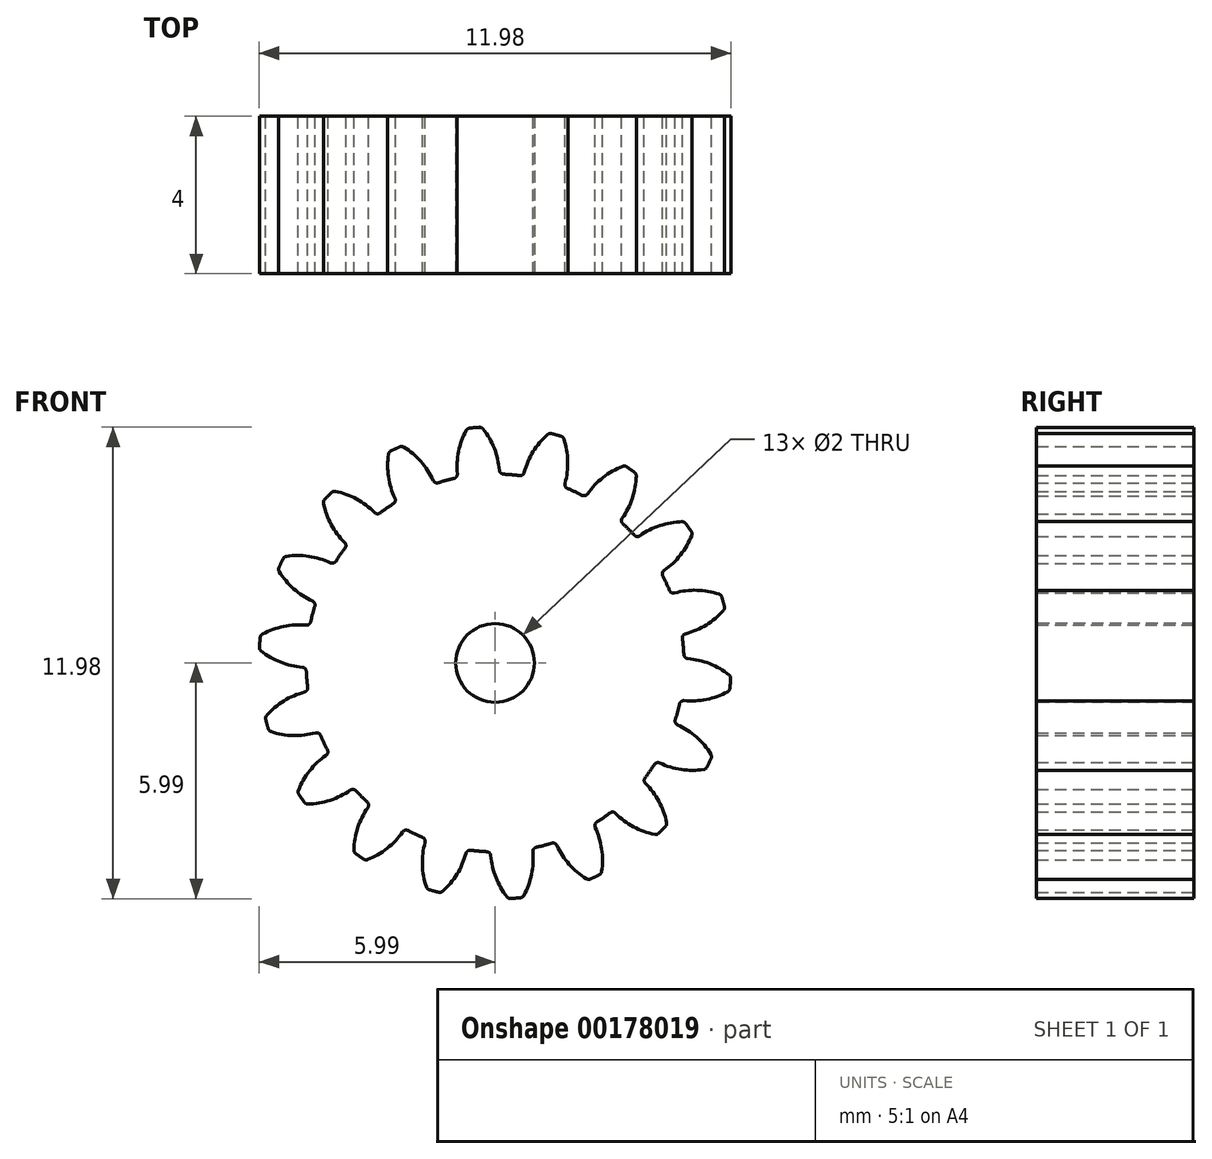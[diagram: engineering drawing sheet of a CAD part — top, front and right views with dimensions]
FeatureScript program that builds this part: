
annotation { "Feature Type Name" : "Feature", "Feature Type Description" : "" }
export const myFeature = defineFeature(function(context is Context, id is Id, definition is map)
    precondition{}
    {
        {
            var Q0;
            Q0=qCreatedBy(makeId("Front.planeOp"),FACE);
            var sketch = newSketch(context, id + "F0", { "sketchPlane" : qUnion([Q0])});
            skCircle(sketch, "E0", {"center": v(0, 0) * mm, "radius": 4.8 * mm, "construction": true});
            skCircle(sketch, "E1", {"center": v(0, 0) * mm, "radius": 5.4 * mm, "construction": true});
            skCircle(sketch, "E2", {"center": v(0, 0) * mm, "radius": 6 * mm, "construction": true});
            skLineSegment(sketch, "E3", {"start": v(0, 0) * mm, "end": v(0, 8.87) * mm, "construction": true});
            skCircle(sketch, "E4.cCircle", {"center": v(0, 0) * mm, "radius": 8.87 * mm, "construction": true});
            skLineSegment(sketch, "E4.0", {"start": v(-0.78, 8.87) * mm, "end": v(0.78, 8.87) * mm, "construction": true});
            skLineSegment(sketch, "E4.1", {"start": v(0.78, 8.87) * mm, "end": v(2.3, 8.6) * mm, "construction": true});
            skLineSegment(sketch, "E4.2", {"start": v(2.3, 8.6) * mm, "end": v(3.76, 8.07) * mm, "construction": true});
            skLineSegment(sketch, "E4.3", {"start": v(3.76, 8.07) * mm, "end": v(5.1, 7.3) * mm, "construction": true});
            skLineSegment(sketch, "E4.4", {"start": v(5.1, 7.3) * mm, "end": v(6.3, 6.3) * mm, "construction": true});
            skLineSegment(sketch, "E4.5", {"start": v(6.3, 6.3) * mm, "end": v(7.3, 5.1) * mm, "construction": true});
            skLineSegment(sketch, "E4.6", {"start": v(7.3, 5.1) * mm, "end": v(8.07, 3.76) * mm, "construction": true});
            skLineSegment(sketch, "E4.7", {"start": v(8.07, 3.76) * mm, "end": v(8.6, 2.3) * mm, "construction": true});
            skLineSegment(sketch, "E4.8", {"start": v(8.6, 2.3) * mm, "end": v(8.87, 0.78) * mm, "construction": true});
            skLineSegment(sketch, "E4.9", {"start": v(8.87, 0.78) * mm, "end": v(8.87, -0.78) * mm, "construction": true});
            skLineSegment(sketch, "E4.10", {"start": v(8.87, -0.78) * mm, "end": v(8.6, -2.3) * mm, "construction": true});
            skLineSegment(sketch, "E4.11", {"start": v(8.6, -2.3) * mm, "end": v(8.07, -3.76) * mm, "construction": true});
            skLineSegment(sketch, "E4.12", {"start": v(8.07, -3.76) * mm, "end": v(7.3, -5.1) * mm, "construction": true});
            skLineSegment(sketch, "E4.13", {"start": v(7.3, -5.1) * mm, "end": v(6.3, -6.3) * mm, "construction": true});
            skLineSegment(sketch, "E4.14", {"start": v(6.3, -6.3) * mm, "end": v(5.1, -7.3) * mm, "construction": true});
            skLineSegment(sketch, "E4.15", {"start": v(5.1, -7.3) * mm, "end": v(3.76, -8.07) * mm, "construction": true});
            skLineSegment(sketch, "E4.16", {"start": v(3.76, -8.07) * mm, "end": v(2.3, -8.6) * mm, "construction": true});
            skLineSegment(sketch, "E4.17", {"start": v(2.3, -8.6) * mm, "end": v(0.78, -8.87) * mm, "construction": true});
            skLineSegment(sketch, "E4.18", {"start": v(0.78, -8.87) * mm, "end": v(-0.78, -8.87) * mm, "construction": true});
            skLineSegment(sketch, "E4.19", {"start": v(-0.78, -8.87) * mm, "end": v(-2.3, -8.6) * mm, "construction": true});
            skLineSegment(sketch, "E4.20", {"start": v(-2.3, -8.6) * mm, "end": v(-3.76, -8.07) * mm, "construction": true});
            skLineSegment(sketch, "E4.21", {"start": v(-3.76, -8.07) * mm, "end": v(-5.1, -7.3) * mm, "construction": true});
            skLineSegment(sketch, "E4.22", {"start": v(-5.1, -7.3) * mm, "end": v(-6.3, -6.3) * mm, "construction": true});
            skLineSegment(sketch, "E4.23", {"start": v(-6.3, -6.3) * mm, "end": v(-7.3, -5.1) * mm, "construction": true});
            skLineSegment(sketch, "E4.24", {"start": v(-7.3, -5.1) * mm, "end": v(-8.07, -3.76) * mm, "construction": true});
            skLineSegment(sketch, "E4.25", {"start": v(-8.07, -3.76) * mm, "end": v(-8.6, -2.3) * mm, "construction": true});
            skLineSegment(sketch, "E4.26", {"start": v(-8.6, -2.3) * mm, "end": v(-8.87, -0.78) * mm, "construction": true});
            skLineSegment(sketch, "E4.27", {"start": v(-8.87, -0.78) * mm, "end": v(-8.87, 0.78) * mm, "construction": true});
            skLineSegment(sketch, "E4.28", {"start": v(-8.87, 0.78) * mm, "end": v(-8.6, 2.3) * mm, "construction": true});
            skLineSegment(sketch, "E4.29", {"start": v(-8.6, 2.3) * mm, "end": v(-8.07, 3.76) * mm, "construction": true});
            skLineSegment(sketch, "E4.30", {"start": v(-8.07, 3.76) * mm, "end": v(-7.3, 5.1) * mm, "construction": true});
            skLineSegment(sketch, "E4.31", {"start": v(-7.3, 5.1) * mm, "end": v(-6.3, 6.3) * mm, "construction": true});
            skLineSegment(sketch, "E4.32", {"start": v(-6.3, 6.3) * mm, "end": v(-5.1, 7.3) * mm, "construction": true});
            skLineSegment(sketch, "E4.33", {"start": v(-5.1, 7.3) * mm, "end": v(-3.76, 8.07) * mm, "construction": true});
            skLineSegment(sketch, "E4.34", {"start": v(-3.76, 8.07) * mm, "end": v(-2.3, 8.6) * mm, "construction": true});
            skLineSegment(sketch, "E4.35", {"start": v(-2.3, 8.6) * mm, "end": v(-0.78, 8.87) * mm, "construction": true});
            skPoint(sketch, "E4.0.midPoint", {"position": v(0, 8.87) * mm});
            skLineSegment(sketch, "E5.0", {"start": v(0, 8.87) * mm, "end": v(1.58, 8.72) * mm, "construction": true});
            skLineSegment(sketch, "E5.1", {"start": v(1.58, 8.72) * mm, "end": v(3.12, 8.3) * mm, "construction": true});
            skLineSegment(sketch, "E5.2", {"start": v(3.12, 8.3) * mm, "end": v(4.55, 7.61) * mm, "construction": true});
            skLineSegment(sketch, "E5.3", {"start": v(4.55, 7.61) * mm, "end": v(5.83, 6.68) * mm, "construction": true});
            skLineSegment(sketch, "E5.4", {"start": v(5.83, 6.68) * mm, "end": v(6.93, 5.53) * mm, "construction": true});
            skLineSegment(sketch, "E5.5", {"start": v(6.93, 5.53) * mm, "end": v(7.8, 4.2) * mm, "construction": true});
            skLineSegment(sketch, "E5.6", {"start": v(7.8, 4.2) * mm, "end": v(8.43, 2.74) * mm, "construction": true});
            skLineSegment(sketch, "E5.7", {"start": v(8.43, 2.74) * mm, "end": v(8.79, 1.2) * mm, "construction": true});
            skLineSegment(sketch, "E5.8", {"start": v(8.79, 1.2) * mm, "end": v(8.86, -0.4) * mm, "construction": true});
            skLineSegment(sketch, "E5.9", {"start": v(8.86, -0.4) * mm, "end": v(8.65, -1.97) * mm, "construction": true});
            skLineSegment(sketch, "E5.10", {"start": v(8.65, -1.97) * mm, "end": v(8.15, -3.49) * mm, "construction": true});
            skLineSegment(sketch, "E5.11", {"start": v(8.15, -3.49) * mm, "end": v(7.4, -4.88) * mm, "construction": true});
            skLineSegment(sketch, "E5.12", {"start": v(7.4, -4.88) * mm, "end": v(6.4, -6.13) * mm, "construction": true});
            skLineSegment(sketch, "E5.13", {"start": v(6.4, -6.13) * mm, "end": v(5.21, -7.17) * mm, "construction": true});
            skLineSegment(sketch, "E5.14", {"start": v(5.21, -7.17) * mm, "end": v(3.85, -7.99) * mm, "construction": true});
            skLineSegment(sketch, "E5.15", {"start": v(3.85, -7.99) * mm, "end": v(2.36, -8.55) * mm, "construction": true});
            skLineSegment(sketch, "E5.16", {"start": v(2.36, -8.55) * mm, "end": v(0.8, -8.83) * mm, "construction": true});
            skLineSegment(sketch, "E5.17", {"start": v(0.8, -8.83) * mm, "end": v(-0.8, -8.83) * mm, "construction": true});
            skLineSegment(sketch, "E5.18", {"start": v(-0.8, -8.83) * mm, "end": v(-2.36, -8.55) * mm, "construction": true});
            skLineSegment(sketch, "E5.19", {"start": v(-2.36, -8.55) * mm, "end": v(-3.85, -7.99) * mm, "construction": true});
            skLineSegment(sketch, "E5.20", {"start": v(-3.85, -7.99) * mm, "end": v(-5.21, -7.17) * mm, "construction": true});
            skLineSegment(sketch, "E5.21", {"start": v(-5.21, -7.17) * mm, "end": v(-6.4, -6.13) * mm, "construction": true});
            skLineSegment(sketch, "E5.22", {"start": v(-6.4, -6.13) * mm, "end": v(-7.4, -4.88) * mm, "construction": true});
            skLineSegment(sketch, "E5.23", {"start": v(-7.4, -4.88) * mm, "end": v(-8.15, -3.49) * mm, "construction": true});
            skLineSegment(sketch, "E5.24", {"start": v(-8.15, -3.49) * mm, "end": v(-8.65, -1.97) * mm, "construction": true});
            skLineSegment(sketch, "E5.25", {"start": v(-8.65, -1.97) * mm, "end": v(-8.86, -0.4) * mm, "construction": true});
            skLineSegment(sketch, "E5.26", {"start": v(-8.86, -0.4) * mm, "end": v(-8.79, 1.2) * mm, "construction": true});
            skLineSegment(sketch, "E5.27", {"start": v(-8.79, 1.2) * mm, "end": v(-8.43, 2.74) * mm, "construction": true});
            skLineSegment(sketch, "E5.28", {"start": v(-8.43, 2.74) * mm, "end": v(-7.8, 4.2) * mm, "construction": true});
            skLineSegment(sketch, "E5.29", {"start": v(-7.8, 4.2) * mm, "end": v(-6.93, 5.53) * mm, "construction": true});
            skLineSegment(sketch, "E5.30", {"start": v(-6.93, 5.53) * mm, "end": v(-5.83, 6.68) * mm, "construction": true});
            skLineSegment(sketch, "E5.31", {"start": v(-5.83, 6.68) * mm, "end": v(-4.55, 7.61) * mm, "construction": true});
            skLineSegment(sketch, "E5.32", {"start": v(-4.55, 7.61) * mm, "end": v(-3.12, 8.3) * mm, "construction": true});
            skLineSegment(sketch, "E5.33", {"start": v(-3.12, 8.3) * mm, "end": v(-1.58, 8.72) * mm, "construction": true});
            skLineSegment(sketch, "E5.34", {"start": v(-1.58, 8.72) * mm, "end": v(0, 8.87) * mm, "construction": true});
            skLineSegment(sketch, "E6", {"start": v(0, 0) * mm, "end": v(-0.78, 8.87) * mm, "construction": true});
            skLineSegment(sketch, "E7", {"start": v(0, 5.4) * mm, "end": v(-9.47, 5.4) * mm, "construction": true});
            skLineSegment(sketch, "E8", {"start": v(0, 5.4) * mm, "end": v(-9.34, 2) * mm, "construction": true});
            skCircle(sketch, "E9", {"center": v(0, 5.4) * mm, "radius": 1.94 * mm, "construction": true});
            skCircle(sketch, "E10", {"center": v(-1.83, 4.74) * mm, "radius": 1.94 * mm, "construction": true});
            skArc(sketch, "E11", {"start": v(-0.3, 5.95) * mm, "mid": v(-0.02, 5.45) * mm, "end": v(0.11, 4.9) * mm});
            skArc(sketch, "E12.MirrorCS", {"start": v(-0.73, 5.9) * mm, "mid": v(-0.93, 5.37) * mm, "end": v(-0.96, 4.8) * mm});
            skArc(sketch, "E13", {"start": v(-0.65, 5.96) * mm, "mid": v(-0.52, 5.98) * mm, "end": v(-0.4, 5.99) * mm});
            skArc(sketch, "E14", {"start": v(-1.04, 4.69) * mm, "mid": v(0.42, -4.78) * mm, "end": v(0.21, 4.8) * mm});
            skPoint(sketch, "E15.visualSharp", {"position": v(-0.95, 4.7) * mm});
            skArc(sketch, "E15.filletArc", {"start": v(-1.04, 4.69) * mm, "mid": v(-0.98, 4.73) * mm, "end": v(-0.96, 4.8) * mm});
            skPoint(sketch, "E16.visualSharp", {"position": v(0.12, 4.8) * mm});
            skArc(sketch, "E16.filletArc", {"start": v(0.11, 4.9) * mm, "mid": v(0.14, 4.83) * mm, "end": v(0.21, 4.8) * mm});
            skPoint(sketch, "E17.visualSharp", {"position": v(-0.7, 5.96) * mm});
            skArc(sketch, "E17.filletArc", {"start": v(-0.65, 5.96) * mm, "mid": v(-0.7, 5.95) * mm, "end": v(-0.73, 5.9) * mm});
            skPoint(sketch, "E18.visualSharp", {"position": v(-0.34, 6) * mm});
            skArc(sketch, "E18.filletArc", {"start": v(-0.3, 5.95) * mm, "mid": v(-0.35, 5.98) * mm, "end": v(-0.4, 5.99) * mm});
            skArc(sketch, "E19.1.0", {"start": v(-2.58, 4.05) * mm, "mid": v(-2.54, 4.1) * mm, "end": v(-2.54, 4.18) * mm});
            skArc(sketch, "E19.1.1", {"start": v(-2.7, 5.3) * mm, "mid": v(-2.7, 4.73) * mm, "end": v(-2.54, 4.18) * mm});
            skArc(sketch, "E19.1.2", {"start": v(-2.65, 5.38) * mm, "mid": v(-2.69, 5.35) * mm, "end": v(-2.7, 5.3) * mm});
            skArc(sketch, "E19.1.3", {"start": v(-2.65, 5.38) * mm, "mid": v(-2.54, 5.44) * mm, "end": v(-2.42, 5.49) * mm});
            skArc(sketch, "E19.1.4", {"start": v(-2.32, 5.48) * mm, "mid": v(-2.37, 5.5) * mm, "end": v(-2.42, 5.49) * mm});
            skArc(sketch, "E19.1.5", {"start": v(-2.32, 5.48) * mm, "mid": v(-1.88, 5.12) * mm, "end": v(-1.57, 4.64) * mm});
            skArc(sketch, "E19.1.6", {"start": v(-1.57, 4.64) * mm, "mid": v(-1.52, 4.58) * mm, "end": v(-1.44, 4.58) * mm});
            skArc(sketch, "E19.2.0", {"start": v(-3.81, 2.92) * mm, "mid": v(-3.79, 3) * mm, "end": v(-3.82, 3.06) * mm});
            skArc(sketch, "E19.2.1", {"start": v(-4.36, 4.06) * mm, "mid": v(-4.16, 3.52) * mm, "end": v(-3.82, 3.06) * mm});
            skArc(sketch, "E19.2.2", {"start": v(-4.33, 4.15) * mm, "mid": v(-4.36, 4.1) * mm, "end": v(-4.36, 4.06) * mm});
            skArc(sketch, "E19.2.3", {"start": v(-4.33, 4.15) * mm, "mid": v(-4.24, 4.24) * mm, "end": v(-4.15, 4.33) * mm});
            skArc(sketch, "E19.2.4", {"start": v(-4.06, 4.36) * mm, "mid": v(-4.1, 4.36) * mm, "end": v(-4.15, 4.33) * mm});
            skArc(sketch, "E19.2.5", {"start": v(-4.06, 4.36) * mm, "mid": v(-3.52, 4.16) * mm, "end": v(-3.06, 3.82) * mm});
            skArc(sketch, "E19.2.6", {"start": v(-3.06, 3.82) * mm, "mid": v(-3, 3.79) * mm, "end": v(-2.92, 3.81) * mm});
            skArc(sketch, "E19.3.0", {"start": v(-4.58, 1.44) * mm, "mid": v(-4.58, 1.52) * mm, "end": v(-4.64, 1.57) * mm});
            skArc(sketch, "E19.3.1", {"start": v(-5.48, 2.32) * mm, "mid": v(-5.12, 1.88) * mm, "end": v(-4.64, 1.57) * mm});
            skArc(sketch, "E19.3.2", {"start": v(-5.49, 2.42) * mm, "mid": v(-5.5, 2.37) * mm, "end": v(-5.48, 2.32) * mm});
            skArc(sketch, "E19.3.3", {"start": v(-5.49, 2.42) * mm, "mid": v(-5.44, 2.54) * mm, "end": v(-5.38, 2.65) * mm});
            skArc(sketch, "E19.3.4", {"start": v(-5.3, 2.7) * mm, "mid": v(-5.35, 2.69) * mm, "end": v(-5.38, 2.65) * mm});
            skArc(sketch, "E19.3.5", {"start": v(-5.3, 2.7) * mm, "mid": v(-4.73, 2.7) * mm, "end": v(-4.18, 2.54) * mm});
            skArc(sketch, "E19.3.6", {"start": v(-4.18, 2.54) * mm, "mid": v(-4.1, 2.54) * mm, "end": v(-4.05, 2.58) * mm});
            skArc(sketch, "E19.4.0", {"start": v(-4.8, -0.21) * mm, "mid": v(-4.83, -0.14) * mm, "end": v(-4.9, -0.11) * mm});
            skArc(sketch, "E19.4.1", {"start": v(-5.95, 0.3) * mm, "mid": v(-5.45, 0.02) * mm, "end": v(-4.9, -0.11) * mm});
            skArc(sketch, "E19.4.2", {"start": v(-5.99, 0.4) * mm, "mid": v(-5.98, 0.35) * mm, "end": v(-5.95, 0.3) * mm});
            skArc(sketch, "E19.4.3", {"start": v(-5.99, 0.4) * mm, "mid": v(-5.98, 0.52) * mm, "end": v(-5.96, 0.65) * mm});
            skArc(sketch, "E19.4.4", {"start": v(-5.9, 0.73) * mm, "mid": v(-5.95, 0.7) * mm, "end": v(-5.96, 0.65) * mm});
            skArc(sketch, "E19.4.5", {"start": v(-5.9, 0.73) * mm, "mid": v(-5.37, 0.93) * mm, "end": v(-4.8, 0.96) * mm});
            skArc(sketch, "E19.4.6", {"start": v(-4.8, 0.96) * mm, "mid": v(-4.73, 0.98) * mm, "end": v(-4.69, 1.04) * mm});
            skArc(sketch, "E19.5.0", {"start": v(-4.43, -1.84) * mm, "mid": v(-4.49, -1.79) * mm, "end": v(-4.56, -1.78) * mm});
            skArc(sketch, "E19.5.1", {"start": v(-5.7, -1.75) * mm, "mid": v(-5.13, -1.85) * mm, "end": v(-4.56, -1.78) * mm});
            skArc(sketch, "E19.5.2", {"start": v(-5.76, -1.67) * mm, "mid": v(-5.74, -1.72) * mm, "end": v(-5.7, -1.75) * mm});
            skArc(sketch, "E19.5.3", {"start": v(-5.76, -1.67) * mm, "mid": v(-5.8, -1.55) * mm, "end": v(-5.83, -1.43) * mm});
            skArc(sketch, "E19.5.4", {"start": v(-5.8, -1.33) * mm, "mid": v(-5.83, -1.38) * mm, "end": v(-5.83, -1.43) * mm});
            skArc(sketch, "E19.5.5", {"start": v(-5.8, -1.33) * mm, "mid": v(-5.37, -0.97) * mm, "end": v(-4.84, -0.74) * mm});
            skArc(sketch, "E19.5.6", {"start": v(-4.84, -0.74) * mm, "mid": v(-4.78, -0.7) * mm, "end": v(-4.76, -0.62) * mm});
            skArc(sketch, "E19.6.0", {"start": v(-3.54, -3.25) * mm, "mid": v(-3.6, -3.21) * mm, "end": v(-3.68, -3.23) * mm});
            skArc(sketch, "E19.6.1", {"start": v(-4.75, -3.59) * mm, "mid": v(-4.19, -3.49) * mm, "end": v(-3.68, -3.23) * mm});
            skArc(sketch, "E19.6.2", {"start": v(-4.84, -3.54) * mm, "mid": v(-4.8, -3.58) * mm, "end": v(-4.75, -3.59) * mm});
            skArc(sketch, "E19.6.3", {"start": v(-4.84, -3.54) * mm, "mid": v(-4.91, -3.44) * mm, "end": v(-4.99, -3.34) * mm});
            skArc(sketch, "E19.6.4", {"start": v(-5, -3.24) * mm, "mid": v(-5, -3.29) * mm, "end": v(-4.99, -3.34) * mm});
            skArc(sketch, "E19.6.5", {"start": v(-5, -3.24) * mm, "mid": v(-4.71, -2.74) * mm, "end": v(-4.3, -2.35) * mm});
            skArc(sketch, "E19.6.6", {"start": v(-4.3, -2.35) * mm, "mid": v(-4.25, -2.29) * mm, "end": v(-4.26, -2.21) * mm});
            skArc(sketch, "E19.7.0", {"start": v(-2.21, -4.26) * mm, "mid": v(-2.29, -4.25) * mm, "end": v(-2.35, -4.3) * mm});
            skArc(sketch, "E19.7.1", {"start": v(-3.24, -5) * mm, "mid": v(-2.74, -4.71) * mm, "end": v(-2.35, -4.3) * mm});
            skArc(sketch, "E19.7.2", {"start": v(-3.34, -4.99) * mm, "mid": v(-3.29, -5) * mm, "end": v(-3.24, -5) * mm});
            skArc(sketch, "E19.7.3", {"start": v(-3.34, -4.99) * mm, "mid": v(-3.44, -4.91) * mm, "end": v(-3.54, -4.84) * mm});
            skArc(sketch, "E19.7.4", {"start": v(-3.59, -4.75) * mm, "mid": v(-3.58, -4.8) * mm, "end": v(-3.54, -4.84) * mm});
            skArc(sketch, "E19.7.5", {"start": v(-3.59, -4.75) * mm, "mid": v(-3.49, -4.19) * mm, "end": v(-3.23, -3.68) * mm});
            skArc(sketch, "E19.7.6", {"start": v(-3.23, -3.68) * mm, "mid": v(-3.21, -3.6) * mm, "end": v(-3.25, -3.54) * mm});
            skArc(sketch, "E19.8.0", {"start": v(-0.62, -4.76) * mm, "mid": v(-0.7, -4.78) * mm, "end": v(-0.74, -4.84) * mm});
            skArc(sketch, "E19.8.1", {"start": v(-1.33, -5.8) * mm, "mid": v(-0.97, -5.37) * mm, "end": v(-0.74, -4.84) * mm});
            skArc(sketch, "E19.8.2", {"start": v(-1.43, -5.83) * mm, "mid": v(-1.38, -5.83) * mm, "end": v(-1.33, -5.8) * mm});
            skArc(sketch, "E19.8.3", {"start": v(-1.43, -5.83) * mm, "mid": v(-1.55, -5.8) * mm, "end": v(-1.67, -5.76) * mm});
            skArc(sketch, "E19.8.4", {"start": v(-1.75, -5.7) * mm, "mid": v(-1.72, -5.74) * mm, "end": v(-1.67, -5.76) * mm});
            skArc(sketch, "E19.8.5", {"start": v(-1.75, -5.7) * mm, "mid": v(-1.85, -5.13) * mm, "end": v(-1.78, -4.56) * mm});
            skArc(sketch, "E19.8.6", {"start": v(-1.78, -4.56) * mm, "mid": v(-1.79, -4.49) * mm, "end": v(-1.84, -4.43) * mm});
            skArc(sketch, "E19.9.0", {"start": v(1.04, -4.69) * mm, "mid": v(0.98, -4.73) * mm, "end": v(0.96, -4.8) * mm});
            skArc(sketch, "E19.9.1", {"start": v(0.73, -5.9) * mm, "mid": v(0.93, -5.37) * mm, "end": v(0.96, -4.8) * mm});
            skArc(sketch, "E19.9.2", {"start": v(0.65, -5.96) * mm, "mid": v(0.7, -5.95) * mm, "end": v(0.73, -5.9) * mm});
            skArc(sketch, "E19.9.3", {"start": v(0.65, -5.96) * mm, "mid": v(0.52, -5.98) * mm, "end": v(0.4, -5.99) * mm});
            skArc(sketch, "E19.9.4", {"start": v(0.3, -5.95) * mm, "mid": v(0.35, -5.98) * mm, "end": v(0.4, -5.99) * mm});
            skArc(sketch, "E19.9.5", {"start": v(0.3, -5.95) * mm, "mid": v(0.02, -5.45) * mm, "end": v(-0.11, -4.9) * mm});
            skArc(sketch, "E19.9.6", {"start": v(-0.11, -4.9) * mm, "mid": v(-0.14, -4.83) * mm, "end": v(-0.21, -4.8) * mm});
            skArc(sketch, "E19.10.0", {"start": v(2.58, -4.05) * mm, "mid": v(2.54, -4.1) * mm, "end": v(2.54, -4.18) * mm});
            skArc(sketch, "E19.10.1", {"start": v(2.7, -5.3) * mm, "mid": v(2.7, -4.73) * mm, "end": v(2.54, -4.18) * mm});
            skArc(sketch, "E19.10.2", {"start": v(2.65, -5.38) * mm, "mid": v(2.69, -5.35) * mm, "end": v(2.7, -5.3) * mm});
            skArc(sketch, "E19.10.3", {"start": v(2.65, -5.38) * mm, "mid": v(2.54, -5.44) * mm, "end": v(2.42, -5.49) * mm});
            skArc(sketch, "E19.10.4", {"start": v(2.32, -5.48) * mm, "mid": v(2.37, -5.5) * mm, "end": v(2.42, -5.49) * mm});
            skArc(sketch, "E19.10.5", {"start": v(2.32, -5.48) * mm, "mid": v(1.88, -5.12) * mm, "end": v(1.57, -4.64) * mm});
            skArc(sketch, "E19.10.6", {"start": v(1.57, -4.64) * mm, "mid": v(1.52, -4.58) * mm, "end": v(1.44, -4.58) * mm});
            skArc(sketch, "E19.11.0", {"start": v(3.81, -2.92) * mm, "mid": v(3.79, -3) * mm, "end": v(3.82, -3.06) * mm});
            skArc(sketch, "E19.11.1", {"start": v(4.36, -4.06) * mm, "mid": v(4.16, -3.52) * mm, "end": v(3.82, -3.06) * mm});
            skArc(sketch, "E19.11.2", {"start": v(4.33, -4.15) * mm, "mid": v(4.36, -4.1) * mm, "end": v(4.36, -4.06) * mm});
            skArc(sketch, "E19.11.3", {"start": v(4.33, -4.15) * mm, "mid": v(4.24, -4.24) * mm, "end": v(4.15, -4.33) * mm});
            skArc(sketch, "E19.11.4", {"start": v(4.06, -4.36) * mm, "mid": v(4.1, -4.36) * mm, "end": v(4.15, -4.33) * mm});
            skArc(sketch, "E19.11.5", {"start": v(4.06, -4.36) * mm, "mid": v(3.52, -4.16) * mm, "end": v(3.06, -3.82) * mm});
            skArc(sketch, "E19.11.6", {"start": v(3.06, -3.82) * mm, "mid": v(3, -3.79) * mm, "end": v(2.92, -3.81) * mm});
            skArc(sketch, "E19.12.0", {"start": v(4.58, -1.44) * mm, "mid": v(4.58, -1.52) * mm, "end": v(4.64, -1.57) * mm});
            skArc(sketch, "E19.12.1", {"start": v(5.48, -2.32) * mm, "mid": v(5.12, -1.88) * mm, "end": v(4.64, -1.57) * mm});
            skArc(sketch, "E19.12.2", {"start": v(5.49, -2.42) * mm, "mid": v(5.5, -2.37) * mm, "end": v(5.48, -2.32) * mm});
            skArc(sketch, "E19.12.3", {"start": v(5.49, -2.42) * mm, "mid": v(5.44, -2.54) * mm, "end": v(5.38, -2.65) * mm});
            skArc(sketch, "E19.12.4", {"start": v(5.3, -2.7) * mm, "mid": v(5.35, -2.69) * mm, "end": v(5.38, -2.65) * mm});
            skArc(sketch, "E19.12.5", {"start": v(5.3, -2.7) * mm, "mid": v(4.73, -2.7) * mm, "end": v(4.18, -2.54) * mm});
            skArc(sketch, "E19.12.6", {"start": v(4.18, -2.54) * mm, "mid": v(4.1, -2.54) * mm, "end": v(4.05, -2.58) * mm});
            skArc(sketch, "E19.13.0", {"start": v(4.8, 0.21) * mm, "mid": v(4.83, 0.14) * mm, "end": v(4.9, 0.11) * mm});
            skArc(sketch, "E19.13.1", {"start": v(5.95, -0.3) * mm, "mid": v(5.45, -0.02) * mm, "end": v(4.9, 0.11) * mm});
            skArc(sketch, "E19.13.2", {"start": v(5.99, -0.4) * mm, "mid": v(5.98, -0.35) * mm, "end": v(5.95, -0.3) * mm});
            skArc(sketch, "E19.13.3", {"start": v(5.99, -0.4) * mm, "mid": v(5.98, -0.52) * mm, "end": v(5.96, -0.65) * mm});
            skArc(sketch, "E19.13.4", {"start": v(5.9, -0.73) * mm, "mid": v(5.95, -0.7) * mm, "end": v(5.96, -0.65) * mm});
            skArc(sketch, "E19.13.5", {"start": v(5.9, -0.73) * mm, "mid": v(5.37, -0.93) * mm, "end": v(4.8, -0.96) * mm});
            skArc(sketch, "E19.13.6", {"start": v(4.8, -0.96) * mm, "mid": v(4.73, -0.98) * mm, "end": v(4.69, -1.04) * mm});
            skArc(sketch, "E19.14.0", {"start": v(4.43, 1.84) * mm, "mid": v(4.49, 1.79) * mm, "end": v(4.56, 1.78) * mm});
            skArc(sketch, "E19.14.1", {"start": v(5.7, 1.75) * mm, "mid": v(5.13, 1.85) * mm, "end": v(4.56, 1.78) * mm});
            skArc(sketch, "E19.14.2", {"start": v(5.76, 1.67) * mm, "mid": v(5.74, 1.72) * mm, "end": v(5.7, 1.75) * mm});
            skArc(sketch, "E19.14.3", {"start": v(5.76, 1.67) * mm, "mid": v(5.8, 1.55) * mm, "end": v(5.83, 1.43) * mm});
            skArc(sketch, "E19.14.4", {"start": v(5.8, 1.33) * mm, "mid": v(5.83, 1.38) * mm, "end": v(5.83, 1.43) * mm});
            skArc(sketch, "E19.14.5", {"start": v(5.8, 1.33) * mm, "mid": v(5.37, 0.97) * mm, "end": v(4.84, 0.74) * mm});
            skArc(sketch, "E19.14.6", {"start": v(4.84, 0.74) * mm, "mid": v(4.78, 0.7) * mm, "end": v(4.76, 0.62) * mm});
            skArc(sketch, "E19.15.0", {"start": v(3.54, 3.25) * mm, "mid": v(3.6, 3.21) * mm, "end": v(3.68, 3.23) * mm});
            skArc(sketch, "E19.15.1", {"start": v(4.75, 3.59) * mm, "mid": v(4.19, 3.49) * mm, "end": v(3.68, 3.23) * mm});
            skArc(sketch, "E19.15.2", {"start": v(4.84, 3.54) * mm, "mid": v(4.8, 3.58) * mm, "end": v(4.75, 3.59) * mm});
            skArc(sketch, "E19.15.3", {"start": v(4.84, 3.54) * mm, "mid": v(4.91, 3.44) * mm, "end": v(4.99, 3.34) * mm});
            skArc(sketch, "E19.15.4", {"start": v(5, 3.24) * mm, "mid": v(5, 3.29) * mm, "end": v(4.99, 3.34) * mm});
            skArc(sketch, "E19.15.5", {"start": v(5, 3.24) * mm, "mid": v(4.71, 2.74) * mm, "end": v(4.3, 2.35) * mm});
            skArc(sketch, "E19.15.6", {"start": v(4.3, 2.35) * mm, "mid": v(4.25, 2.29) * mm, "end": v(4.26, 2.21) * mm});
            skArc(sketch, "E19.16.0", {"start": v(2.21, 4.26) * mm, "mid": v(2.29, 4.25) * mm, "end": v(2.35, 4.3) * mm});
            skArc(sketch, "E19.16.1", {"start": v(3.24, 5) * mm, "mid": v(2.74, 4.71) * mm, "end": v(2.35, 4.3) * mm});
            skArc(sketch, "E19.16.2", {"start": v(3.34, 4.99) * mm, "mid": v(3.29, 5) * mm, "end": v(3.24, 5) * mm});
            skArc(sketch, "E19.16.3", {"start": v(3.34, 4.99) * mm, "mid": v(3.44, 4.91) * mm, "end": v(3.54, 4.84) * mm});
            skArc(sketch, "E19.16.4", {"start": v(3.59, 4.75) * mm, "mid": v(3.58, 4.8) * mm, "end": v(3.54, 4.84) * mm});
            skArc(sketch, "E19.16.5", {"start": v(3.59, 4.75) * mm, "mid": v(3.49, 4.19) * mm, "end": v(3.23, 3.68) * mm});
            skArc(sketch, "E19.16.6", {"start": v(3.23, 3.68) * mm, "mid": v(3.21, 3.6) * mm, "end": v(3.25, 3.54) * mm});
            skArc(sketch, "E19.17.0", {"start": v(0.62, 4.76) * mm, "mid": v(0.7, 4.78) * mm, "end": v(0.74, 4.84) * mm});
            skArc(sketch, "E19.17.1", {"start": v(1.33, 5.8) * mm, "mid": v(0.97, 5.37) * mm, "end": v(0.74, 4.84) * mm});
            skArc(sketch, "E19.17.2", {"start": v(1.43, 5.83) * mm, "mid": v(1.38, 5.83) * mm, "end": v(1.33, 5.8) * mm});
            skArc(sketch, "E19.17.3", {"start": v(1.43, 5.83) * mm, "mid": v(1.55, 5.8) * mm, "end": v(1.67, 5.76) * mm});
            skArc(sketch, "E19.17.4", {"start": v(1.75, 5.7) * mm, "mid": v(1.72, 5.74) * mm, "end": v(1.67, 5.76) * mm});
            skArc(sketch, "E19.17.5", {"start": v(1.75, 5.7) * mm, "mid": v(1.85, 5.13) * mm, "end": v(1.78, 4.56) * mm});
            skArc(sketch, "E19.17.6", {"start": v(1.78, 4.56) * mm, "mid": v(1.79, 4.49) * mm, "end": v(1.84, 4.43) * mm});
            skSolve(sketch);
        }
        {
            var Q0;
            Q0=qSketchRegion(id+"F0",true);
            extrude(context, id + "F1", {"entities" : qUnion([Q0]), "depth" : 4 * mm});
        }
        {
            var Q0;
            Q0=makeQuery(id+"F1.opExtrude","CAP_FACE",FACE,{"disambiguationData":[OSD([sQuery(id+"F0.wireOp",EDGE,"E11"),sQuery(id+"F0.wireOp",EDGE,"E12.MirrorCS"),sQuery(id+"F0.wireOp",EDGE,"E13"),sQuery(id+"F0.wireOp",EDGE,"E14"),sQuery(id+"F0.wireOp",EDGE,"E15.filletArc"),sQuery(id+"F0.wireOp",EDGE,"E16.filletArc"),sQuery(id+"F0.wireOp",EDGE,"E17.filletArc"),sQuery(id+"F0.wireOp",EDGE,"E18.filletArc"),sQuery(id+"F0.wireOp",EDGE,"E19.1.0"),sQuery(id+"F0.wireOp",EDGE,"E19.1.1"),sQuery(id+"F0.wireOp",EDGE,"E19.1.2"),sQuery(id+"F0.wireOp",EDGE,"E19.1.3"),sQuery(id+"F0.wireOp",EDGE,"E19.1.4"),sQuery(id+"F0.wireOp",EDGE,"E19.1.5"),sQuery(id+"F0.wireOp",EDGE,"E19.1.6"),sQuery(id+"F0.wireOp",EDGE,"E19.2.0"),sQuery(id+"F0.wireOp",EDGE,"E19.2.1"),sQuery(id+"F0.wireOp",EDGE,"E19.2.2"),sQuery(id+"F0.wireOp",EDGE,"E19.2.3"),sQuery(id+"F0.wireOp",EDGE,"E19.2.4"),sQuery(id+"F0.wireOp",EDGE,"E19.2.5"),sQuery(id+"F0.wireOp",EDGE,"E19.2.6"),sQuery(id+"F0.wireOp",EDGE,"E19.3.0"),sQuery(id+"F0.wireOp",EDGE,"E19.3.1"),sQuery(id+"F0.wireOp",EDGE,"E19.3.2"),sQuery(id+"F0.wireOp",EDGE,"E19.3.3"),sQuery(id+"F0.wireOp",EDGE,"E19.3.4"),sQuery(id+"F0.wireOp",EDGE,"E19.3.5"),sQuery(id+"F0.wireOp",EDGE,"E19.3.6"),sQuery(id+"F0.wireOp",EDGE,"E19.4.0"),sQuery(id+"F0.wireOp",EDGE,"E19.4.1"),sQuery(id+"F0.wireOp",EDGE,"E19.4.2"),sQuery(id+"F0.wireOp",EDGE,"E19.4.3"),sQuery(id+"F0.wireOp",EDGE,"E19.4.4"),sQuery(id+"F0.wireOp",EDGE,"E19.4.5"),sQuery(id+"F0.wireOp",EDGE,"E19.4.6"),sQuery(id+"F0.wireOp",EDGE,"E19.5.0"),sQuery(id+"F0.wireOp",EDGE,"E19.5.1"),sQuery(id+"F0.wireOp",EDGE,"E19.5.2"),sQuery(id+"F0.wireOp",EDGE,"E19.5.3"),sQuery(id+"F0.wireOp",EDGE,"E19.5.4"),sQuery(id+"F0.wireOp",EDGE,"E19.5.5"),sQuery(id+"F0.wireOp",EDGE,"E19.5.6"),sQuery(id+"F0.wireOp",EDGE,"E19.6.0"),sQuery(id+"F0.wireOp",EDGE,"E19.6.1"),sQuery(id+"F0.wireOp",EDGE,"E19.6.2"),sQuery(id+"F0.wireOp",EDGE,"E19.6.3"),sQuery(id+"F0.wireOp",EDGE,"E19.6.4"),sQuery(id+"F0.wireOp",EDGE,"E19.6.5"),sQuery(id+"F0.wireOp",EDGE,"E19.6.6"),sQuery(id+"F0.wireOp",EDGE,"E19.7.0"),sQuery(id+"F0.wireOp",EDGE,"E19.7.1"),sQuery(id+"F0.wireOp",EDGE,"E19.7.2"),sQuery(id+"F0.wireOp",EDGE,"E19.7.3"),sQuery(id+"F0.wireOp",EDGE,"E19.7.4"),sQuery(id+"F0.wireOp",EDGE,"E19.7.5"),sQuery(id+"F0.wireOp",EDGE,"E19.7.6"),sQuery(id+"F0.wireOp",EDGE,"E19.8.0"),sQuery(id+"F0.wireOp",EDGE,"E19.8.1"),sQuery(id+"F0.wireOp",EDGE,"E19.8.2"),sQuery(id+"F0.wireOp",EDGE,"E19.8.3"),sQuery(id+"F0.wireOp",EDGE,"E19.8.4"),sQuery(id+"F0.wireOp",EDGE,"E19.8.5"),sQuery(id+"F0.wireOp",EDGE,"E19.8.6"),sQuery(id+"F0.wireOp",EDGE,"E19.9.0"),sQuery(id+"F0.wireOp",EDGE,"E19.9.1"),sQuery(id+"F0.wireOp",EDGE,"E19.9.2"),sQuery(id+"F0.wireOp",EDGE,"E19.9.3"),sQuery(id+"F0.wireOp",EDGE,"E19.9.4"),sQuery(id+"F0.wireOp",EDGE,"E19.9.5"),sQuery(id+"F0.wireOp",EDGE,"E19.9.6"),sQuery(id+"F0.wireOp",EDGE,"E19.10.0"),sQuery(id+"F0.wireOp",EDGE,"E19.10.1"),sQuery(id+"F0.wireOp",EDGE,"E19.10.2"),sQuery(id+"F0.wireOp",EDGE,"E19.10.3"),sQuery(id+"F0.wireOp",EDGE,"E19.10.4"),sQuery(id+"F0.wireOp",EDGE,"E19.10.5"),sQuery(id+"F0.wireOp",EDGE,"E19.10.6"),sQuery(id+"F0.wireOp",EDGE,"E19.11.0"),sQuery(id+"F0.wireOp",EDGE,"E19.11.1"),sQuery(id+"F0.wireOp",EDGE,"E19.11.2"),sQuery(id+"F0.wireOp",EDGE,"E19.11.3"),sQuery(id+"F0.wireOp",EDGE,"E19.11.4"),sQuery(id+"F0.wireOp",EDGE,"E19.11.5"),sQuery(id+"F0.wireOp",EDGE,"E19.11.6"),sQuery(id+"F0.wireOp",EDGE,"E19.12.0"),sQuery(id+"F0.wireOp",EDGE,"E19.12.1"),sQuery(id+"F0.wireOp",EDGE,"E19.12.2"),sQuery(id+"F0.wireOp",EDGE,"E19.12.3"),sQuery(id+"F0.wireOp",EDGE,"E19.12.4"),sQuery(id+"F0.wireOp",EDGE,"E19.12.5"),sQuery(id+"F0.wireOp",EDGE,"E19.12.6"),sQuery(id+"F0.wireOp",EDGE,"E19.13.0"),sQuery(id+"F0.wireOp",EDGE,"E19.13.1"),sQuery(id+"F0.wireOp",EDGE,"E19.13.2"),sQuery(id+"F0.wireOp",EDGE,"E19.13.3"),sQuery(id+"F0.wireOp",EDGE,"E19.13.4"),sQuery(id+"F0.wireOp",EDGE,"E19.13.5"),sQuery(id+"F0.wireOp",EDGE,"E19.13.6"),sQuery(id+"F0.wireOp",EDGE,"E19.14.0"),sQuery(id+"F0.wireOp",EDGE,"E19.14.1"),sQuery(id+"F0.wireOp",EDGE,"E19.14.2"),sQuery(id+"F0.wireOp",EDGE,"E19.14.3"),sQuery(id+"F0.wireOp",EDGE,"E19.14.4"),sQuery(id+"F0.wireOp",EDGE,"E19.14.5"),sQuery(id+"F0.wireOp",EDGE,"E19.14.6"),sQuery(id+"F0.wireOp",EDGE,"E19.15.0"),sQuery(id+"F0.wireOp",EDGE,"E19.15.1"),sQuery(id+"F0.wireOp",EDGE,"E19.15.2"),sQuery(id+"F0.wireOp",EDGE,"E19.15.3"),sQuery(id+"F0.wireOp",EDGE,"E19.15.4"),sQuery(id+"F0.wireOp",EDGE,"E19.15.5"),sQuery(id+"F0.wireOp",EDGE,"E19.15.6"),sQuery(id+"F0.wireOp",EDGE,"E19.16.0"),sQuery(id+"F0.wireOp",EDGE,"E19.16.1"),sQuery(id+"F0.wireOp",EDGE,"E19.16.2"),sQuery(id+"F0.wireOp",EDGE,"E19.16.3"),sQuery(id+"F0.wireOp",EDGE,"E19.16.4"),sQuery(id+"F0.wireOp",EDGE,"E19.16.5"),sQuery(id+"F0.wireOp",EDGE,"E19.16.6"),sQuery(id+"F0.wireOp",EDGE,"E19.17.0"),sQuery(id+"F0.wireOp",EDGE,"E19.17.1"),sQuery(id+"F0.wireOp",EDGE,"E19.17.2"),sQuery(id+"F0.wireOp",EDGE,"E19.17.3"),sQuery(id+"F0.wireOp",EDGE,"E19.17.4"),sQuery(id+"F0.wireOp",EDGE,"E19.17.5"),sQuery(id+"F0.wireOp",EDGE,"E19.17.6")])],"isStart":false});
            var sketch = newSketch(context, id + "F2", { "sketchPlane" : qUnion([Q0])});
            skCircle(sketch, "E20", {"center": v(0, 0) * mm, "radius": 1 * mm});
            skSolve(sketch);
        }
        {
            var Q0;
            Q0=qSketchRegion(id+"F2",true);
            extrude(context, id + "F3", {"entities" : qUnion([Q0]), "operationType" : NewBodyOperationType.REMOVE, "oppositeDirection" : true, "depth" : 25 * mm});
        }
    });
